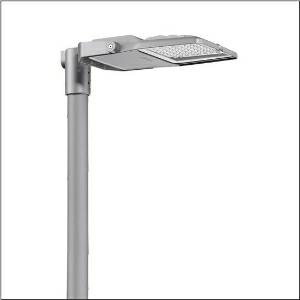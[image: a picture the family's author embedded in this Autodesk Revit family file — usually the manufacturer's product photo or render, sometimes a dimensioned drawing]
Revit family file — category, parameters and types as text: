
# Revit family: floodlight_fl_21_iq_mini___pl64_5xa7771b4e3a_3408
name_source: partatom
category: Lighting Fixtures
units: mm (PartAtom-declared; Revit-internal decimal feet)

## family parameters
Cut with Voids When Loaded = No
Host = Face
Light Source = No
Part Type = Normal
Room Calculation Point = No
Round Connector Dimension = Use Diameter
Shared = No

## types (1)
- --- (1 x LED, 6270 lm, 45.5 W, 4000K)
    Apparent Load = 46 VA
    CIE Flux Codes = 28 80 98 100 100
    Color Rendering = 70
    Color Temperature = 4000K
    Default Elevation = 1800 mm
    Description = Floodlight FL 21 iQ mini, floodlight, primary light control with lens, of PMMA, primary optical cover: protective disc, of toughened safety glass, transparent, light distribution: PL64, light emission: direct distribution, installation type: surface-mounted, LED, High Power LED, rated luminous flux: 6.270lm, luminous efficacy: 138lm/W, light colour: 740, colour temperature: 4000K, control gear: iQ Comfort/DALI, control: Auto-Match, Temp-Guard, Lumen-Switch, Night-Set, Smart-Wire, Light-Fading, Desk-Remote (wireless, voltage-free reading and setting of iQ features in the workshop via application-optimized NFC function/RFID function), optimised constant luminous flux control (CLO 2.0), with terminal, 6-pole, mains connection: 220..240V, AC, 50/60Hz, start of lifetime: 46W, end of service life: 48W, reduction: 22W, luminaire housing, of diecast aluminium, powder-coated, Siteco® metallic grey (DB 702S), corrosivity category C5 mid according to DIN EN ISO 12944, suitable for swimming pools, chlorine-resistant, sealing non-destructively replaceable, please order mast flange separately, mast bracket, of steel, galvanised, powder-coated, Siteco® metallic grey (DB 702S), protection rating (complete): IP66, insulation class (complete): insulation class II (safety insulation), certification: CE, ENEC, VDE, protection symbol: D, impact resistance: IK08, permissible operating ambient temperature: -40..+40°C, permissible operating ambient temperature for outdoor applications: -40..+50°C, standard: DIN EN 12944, LABS conformity tested according to VDMA 24364:2018-05, packaging unit: 1 piece

Light Distribution: PL64
    Height = 70 mm
    Lamp = 1 x LED
    Lamp Light Flux = 6270 lm
    Lamp Power = 45.5 W
    Lamp count = 1
    Length = 485 mm
    Luminous efficacy = 138 lm/W
    Manufacturer = Siteco
    ModVariant = No
    Model = 5XA7771B4E3A
    Number of Poles = 1
    OnlyDefault = Yes
    Power Factor = 1
    Product Name = Floodlight FL 21 iQ mini | PL64
    Product group = floodlight | pylon annexe
    ProductGroupID = 6201
    Protection Class = Protection class II
    Protection Degree = IP 66
    RLX_Detail_Level = 1
    RLX_Emergency_Light_Flux = 0 lm
    RLX_Emergency_Type = 0
    RLX_Emergency_Type_DB = No
    RlxData = <blob elided: 101329 chars, md5=f59c9d98>
    Socket = socket
    Standby Power = 0 W
    System Light Flux = 6270 lm
    System Power = 46 W
    Type Comments = factory setting: luminous flux: 100 % | dim-lin: 254 | 463 mA
    Type Image = l_1007125.jpg
    URL = http://relux.com
    VarID = @adj_188511
    Voltage = 0 V
    Weight = 0.00 kg
    Width = 337 mm

## geometry (parser evidence)
native form markers: Blend x4, Sweep x13
no freeform markers — native parametric forms only
